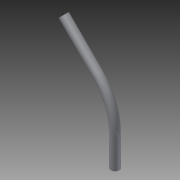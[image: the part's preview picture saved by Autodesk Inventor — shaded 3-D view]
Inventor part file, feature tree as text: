
AUTODESK INVENTOR PART (.ipt)
format: ipt  version: 2014 SP1 (Build 180222100, 222)  size: 118,272 bytes
history: native  units: in
note: dims shown in document units (in); Inventor stores cm internally (conversion verified against a paired STEP export)
features: reference x5, sketch x2, plane x1, sweep x1
ambient origin geometry x8: Origin, YZ Plane, XZ Plane, XY Plane, X Axis, Y Axis, Z Axis, Center Point
bodies: Solid1 (feature_tree)
feature tree (9):
  sketch  "Sketch1"  dims[d0=0.7274in d1=0.5in]
  plane  "Work Plane1"
  sweep  "Sweep1"
  reference  "Reference1"
  reference  "Reference2"
  reference  "Reference3"
  reference  "Reference4"
  sketch  "Sketch2"  dims[d2=0.7274in d3=0.0in d4=0.45in]
  reference  "Reference5"
